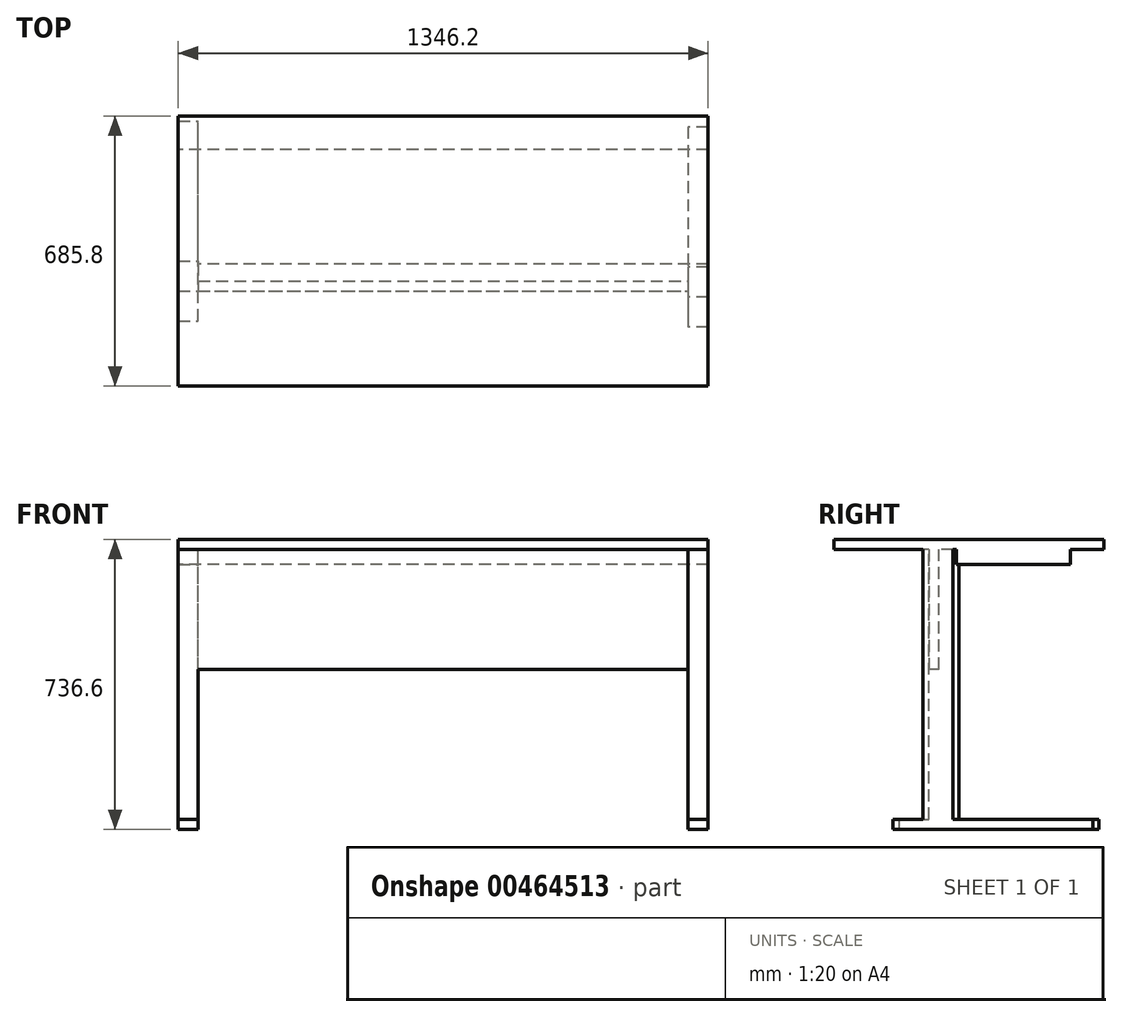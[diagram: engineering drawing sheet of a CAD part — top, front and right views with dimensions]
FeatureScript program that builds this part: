
annotation { "Feature Type Name" : "Feature", "Feature Type Description" : "" }
export const myFeature = defineFeature(function(context is Context, id is Id, definition is map)
    precondition{}
    {
        {
            var Q0;
            Q0=qCreatedBy(makeId("Top.planeOp"),FACE);
            var sketch = newSketch(context, id + "F0", { "sketchPlane" : qUnion([Q0])});
            skLineSegment(sketch, "E0.bottom", {"start": v(-674.77, 339.47) * mm, "end": v(671.43, 339.47) * mm});
            skLineSegment(sketch, "E0.top", {"start": v(-674.77, -346.33) * mm, "end": v(671.43, -346.33) * mm});
            skLineSegment(sketch, "E0.left", {"start": v(-674.77, 339.47) * mm, "end": v(-674.77, -346.33) * mm});
            skLineSegment(sketch, "E0.right", {"start": v(671.43, 339.47) * mm, "end": v(671.43, -346.33) * mm});
            skSolve(sketch);
        }
        {
            var Q0;
            Q0=makeQuery(id+"F0.imprint","IMPRINT",FACE,{"disambiguationData":[TD([[makeQuery(id+"F0.imprint","IMPRINT",EDGE,{"derivedFrom":sQuery(id+"F0.wireOp",EDGE,"E0.bottom")}),-1.0]])]});
            extrude(context, id + "F1", {"entities" : qUnion([Q0]), "depth" : 25.4 * mm});
        }
        {
            var Q0;
            Q0=makeQuery(id+"F1.opExtrude","CAP_FACE",FACE,{"disambiguationData":[OSD([sQuery(id+"F0.wireOp",EDGE,"E0.bottom"),sQuery(id+"F0.wireOp",EDGE,"E0.top"),sQuery(id+"F0.wireOp",EDGE,"E0.left"),sQuery(id+"F0.wireOp",EDGE,"E0.right")])],"isStart":true});
            var sketch = newSketch(context, id + "F2", { "sketchPlane" : qUnion([Q0])});
            skLineSegment(sketch, "E1.bottom", {"start": v(671.43, 43.75) * mm, "end": v(620.63, 43.75) * mm});
            skLineSegment(sketch, "E1.top", {"start": v(671.43, 119.95) * mm, "end": v(620.63, 119.95) * mm});
            skLineSegment(sketch, "E1.left", {"start": v(671.43, 43.75) * mm, "end": v(671.43, 119.95) * mm});
            skLineSegment(sketch, "E1.right", {"start": v(620.63, 43.75) * mm, "end": v(620.63, 119.95) * mm});
            skLineSegment(sketch, "E2.bottom", {"start": v(-674.77, 28.7) * mm, "end": v(-623.97, 28.7) * mm});
            skLineSegment(sketch, "E2.top", {"start": v(-674.77, 104.9) * mm, "end": v(-623.97, 104.9) * mm});
            skLineSegment(sketch, "E2.left", {"start": v(-674.77, 28.7) * mm, "end": v(-674.77, 104.9) * mm});
            skLineSegment(sketch, "E2.right", {"start": v(-623.97, 28.7) * mm, "end": v(-623.97, 104.9) * mm});
            skSolve(sketch);
        }
        {
            var Q0;
            {var subQ6=sQuery(id+"F2.wireOp",EDGE,"E1.bottom");Q0=makeQuery(id+"F2.imprint","IMPRINT",FACE,{"disambiguationData":[TD([[makeQuery(id+"F2.imprint","IMPRINT",EDGE,{"derivedFrom":subQ6}),1.0]])]});}
            var sketch = newSketch(context, id + "F3", { "sketchPlane" : qUnion([Q0])});
            skLineSegment(sketch, "E3.bottom", {"start": v(673.06, -254.3) * mm, "end": v(-675.7, -254.3) * mm});
            skLineSegment(sketch, "E3.top", {"start": v(673.06, 35.86) * mm, "end": v(-675.7, 35.86) * mm});
            skLineSegment(sketch, "E3.left", {"start": v(673.06, -254.3) * mm, "end": v(673.06, 35.86) * mm});
            skLineSegment(sketch, "E3.right", {"start": v(-675.7, -254.3) * mm, "end": v(-675.7, 35.86) * mm});
            skSolve(sketch);
        }
        {
            var Q0;
            {var subQ1=sQuery(id+"F2.wireOp",EDGE,"E2.bottom");var subQ2=makeQuery(id+"F2.imprint","IMPRINT",EDGE,{"derivedFrom":subQ1});Q0=makeQuery(id+"F3.imprint","IMPRINT",FACE,{"disambiguationData":[TD([[makeQuery(id+"F3.imprint","IMPRINT",EDGE,{"derivedFrom":subQ2}),-1.0]])]});}
            extrude(context, id + "F4", {"entities" : qUnion([Q0]), "operationType" : NewBodyOperationType.ADD, "depth" : 38.1 * mm});
        }
        {
            var Q0;
            Q0=makeQuery(id+"F2.imprint","IMPRINT",FACE,{"disambiguationData":[TD([[makeQuery(id+"F2.imprint","IMPRINT",EDGE,{"derivedFrom":sQuery(id+"F2.wireOp",EDGE,"E1.bottom")}),-1.0]])]});
            var Q1;
            Q1=makeQuery(id+"F2.imprint","IMPRINT",FACE,{"disambiguationData":[TD([[makeQuery(id+"F2.imprint","IMPRINT",EDGE,{"derivedFrom":sQuery(id+"F2.wireOp",EDGE,"E2.bottom")}),1.0]])]});
            extrude(context, id + "F5", {"entities" : qUnion([Q0, Q1]), "operationType" : NewBodyOperationType.ADD, "depth" : 685.8 * mm});
        }
        {
            var Q0;
            Q0=makeQuery(id+"F5.opExtrude","SWEPT_FACE",FACE,{"disambiguationData":[OSD([sQuery(id+"F2.wireOp",EDGE,"E1.top")])]});
            var sketch = newSketch(context, id + "F6", { "sketchPlane" : qUnion([Q0])});
            skLineSegment(sketch, "E4.bottom", {"start": v(620.63, -685.8) * mm, "end": v(671.43, -685.8) * mm});
            skLineSegment(sketch, "E4.top", {"start": v(620.63, -711.2) * mm, "end": v(671.43, -711.2) * mm});
            skLineSegment(sketch, "E4.left", {"start": v(620.63, -685.8) * mm, "end": v(620.63, -711.2) * mm});
            skLineSegment(sketch, "E4.right", {"start": v(671.43, -685.8) * mm, "end": v(671.43, -711.2) * mm});
            skSolve(sketch);
        }
        {
            var Q0;
            Q0=makeQuery(id+"F5.opExtrude","SWEPT_FACE",FACE,{"disambiguationData":[OSD([sQuery(id+"F2.wireOp",EDGE,"E2.top")])]});
            var sketch = newSketch(context, id + "F7", { "sketchPlane" : qUnion([Q0])});
            skLineSegment(sketch, "E5.bottom", {"start": v(-674.77, -685.8) * mm, "end": v(-623.97, -685.8) * mm});
            skLineSegment(sketch, "E5.top", {"start": v(-674.77, -711.2) * mm, "end": v(-623.97, -711.2) * mm});
            skLineSegment(sketch, "E5.left", {"start": v(-674.77, -685.8) * mm, "end": v(-674.77, -711.2) * mm});
            skLineSegment(sketch, "E5.right", {"start": v(-623.97, -685.8) * mm, "end": v(-623.97, -711.2) * mm});
            skSolve(sketch);
        }
        {
            var Q0;
            Q0 = qSketchRegion(id + "F7", true);
            extrude(context, id + "F8", {"entities" : qUnion([Q0]), "operationType" : NewBodyOperationType.ADD, "depth" : 76.2 * mm, "hasSecondDirection" : true, "secondDirectionOppositeDirection" : true, "secondDirectionDepth" : 431.8 * mm});
        }
        {
            var Q0;
            Q0=makeQuery(id+"F5.opExtrude","SWEPT_FACE",FACE,{"disambiguationData":[OSD([sQuery(id+"F2.wireOp",EDGE,"E2.top")])]});
            var sketch = newSketch(context, id + "F9", { "sketchPlane" : qUnion([Q0])});
            skLineSegment(sketch, "E6.bottom", {"start": v(-623.97, 0) * mm, "end": v(620.63, 0) * mm});
            skLineSegment(sketch, "E6.top", {"start": v(-623.97, -304.8) * mm, "end": v(620.63, -304.8) * mm});
            skLineSegment(sketch, "E6.left", {"start": v(-623.97, 0) * mm, "end": v(-623.97, -304.8) * mm});
            skLineSegment(sketch, "E6.right", {"start": v(620.63, 0) * mm, "end": v(620.63, -304.8) * mm});
            skSolve(sketch);
        }
        {
            var Q0;
            Q0 = qSketchRegion(id + "F9", true);
            extrude(context, id + "F10", {"entities" : qUnion([Q0]), "operationType" : NewBodyOperationType.ADD, "oppositeDirection" : true, "depth" : 25.4 * mm});
        }
        {
            var Q0;
            Q0=makeQuery(id+"F6.imprint","IMPRINT",FACE,{"disambiguationData":[TD([[makeQuery(id+"F6.imprint","IMPRINT",EDGE,{"derivedFrom":sQuery(id+"F6.wireOp",EDGE,"E4.bottom")}),1.0]])]});
            extrude(context, id + "F11", {"entities" : qUnion([Q0]), "operationType" : NewBodyOperationType.ADD, "oppositeDirection" : true, "depth" : 431.8 * mm, "hasSecondDirection" : true, "secondDirectionOppositeDirection" : false, "secondDirectionDepth" : 76.2 * mm});
        }
    });
